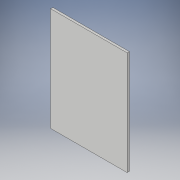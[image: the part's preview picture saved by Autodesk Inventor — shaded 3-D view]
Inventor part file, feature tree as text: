
AUTODESK INVENTOR PART (.ipt)
format: ipt  version: 2017 (Build 210142000, 142)  size: 89,088 bytes
history: native  units: in
note: dims shown in document units (in); Inventor stores cm internally (conversion verified against a paired STEP export)
features: extrude x1, sketch x1
ambient origin geometry x8: Origin, YZ Plane, XZ Plane, XY Plane, X Axis, Y Axis, Z Axis, Center Point
bodies: Solid1 (feature_tree)
feature tree (2):
  extrude  "Extrusion1"  Depth=11.425in
  sketch  "Sketch1"  dims[d0=8.4252in d1=11.425in d2=0.25in d3=0.0in]
